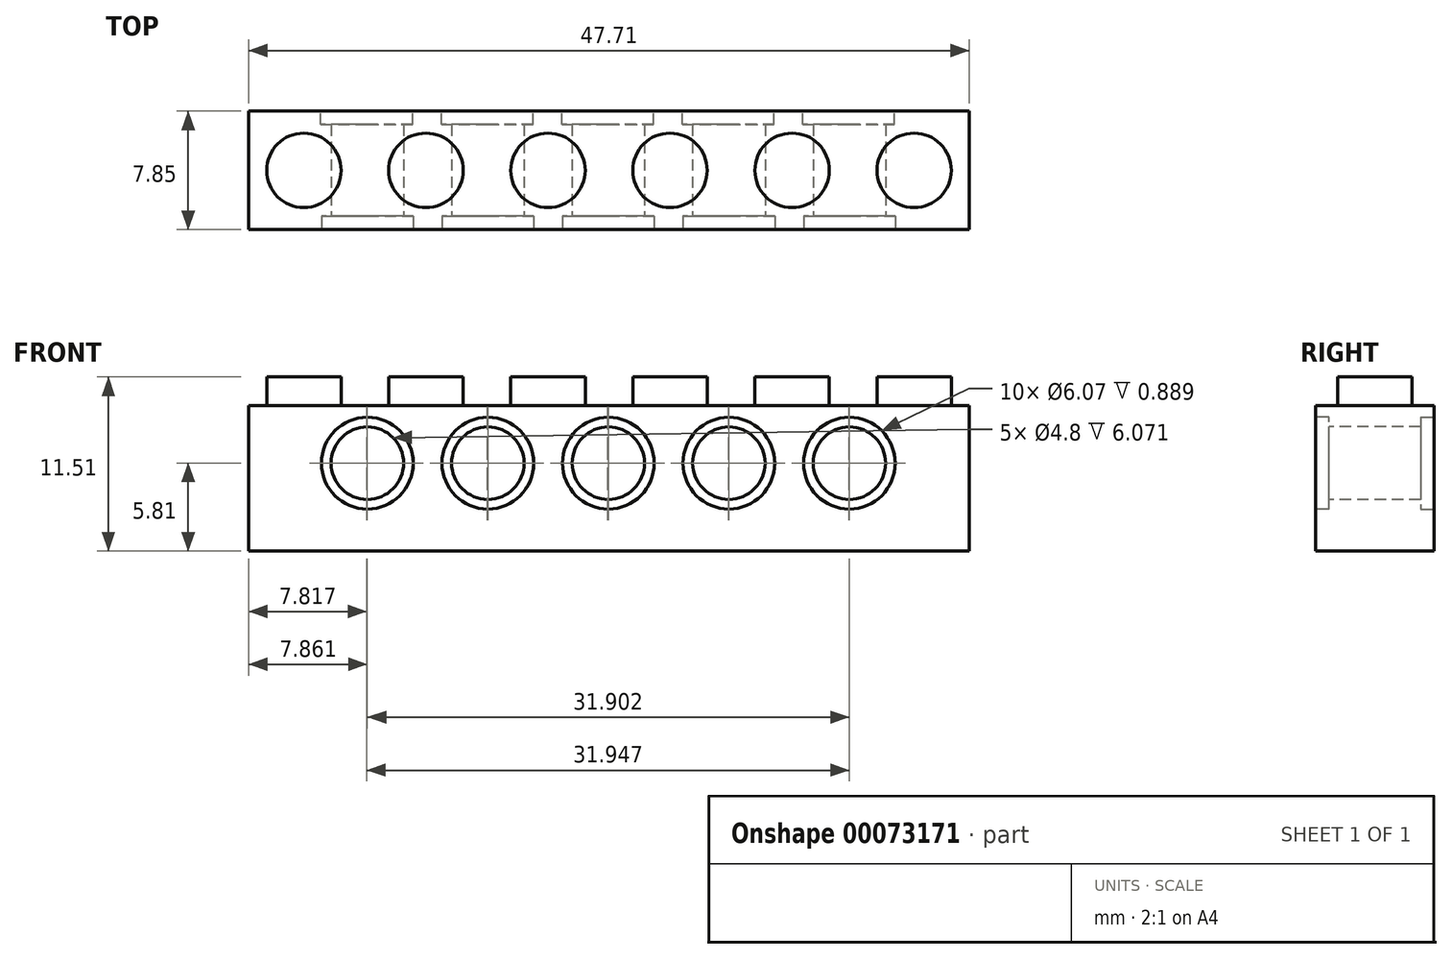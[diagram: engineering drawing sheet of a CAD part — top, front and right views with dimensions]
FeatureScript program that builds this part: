
annotation { "Feature Type Name" : "Feature", "Feature Type Description" : "" }
export const myFeature = defineFeature(function(context is Context, id is Id, definition is map)
    precondition{}
    {
        {
            var Q0;
            Q0=qCreatedBy(makeId("Front.planeOp"),FACE);
            var sketch = newSketch(context, id + "F0", { "sketchPlane" : qUnion([Q0])});
            skLineSegment(sketch, "E0.bottom", {"start": v(-30.48, 15.74) * mm, "end": v(17.23, 15.74) * mm});
            skLineSegment(sketch, "E0.top", {"start": v(-30.48, 6.13) * mm, "end": v(17.23, 6.13) * mm});
            skLineSegment(sketch, "E0.left", {"start": v(-30.48, 15.74) * mm, "end": v(-30.48, 6.13) * mm});
            skLineSegment(sketch, "E0.right", {"start": v(17.23, 15.74) * mm, "end": v(17.23, 6.13) * mm});
            skSolve(sketch);
        }
        {
            var Q0;
            Q0 = qSketchRegion(id + "F0", true);
            extrude(context, id + "F1", {"entities" : qUnion([Q0]), "depth" : 7.85 * mm});
        }
        {
            var Q0;
            Q0=makeQuery(id+"F1.opExtrude","CAP_FACE",FACE,{"disambiguationData":[OSD([sQuery(id+"F0.wireOp",EDGE,"E0.bottom"),sQuery(id+"F0.wireOp",EDGE,"E0.top"),sQuery(id+"F0.wireOp",EDGE,"E0.left"),sQuery(id+"F0.wireOp",EDGE,"E0.right")])],"isStart":false});
            var sketch = newSketch(context, id + "F2", { "sketchPlane" : qUnion([Q0])});
            skCircle(sketch, "E1", {"center": v(-22.62, 11.94) * mm, "radius": 3.04 * mm});
            skPoint(sketch, "E2.centerSnap0", {"position": v(-30.48, 10.93) * mm});
            skCircle(sketch, "E3", {"center": v(-14.64, 11.94) * mm, "radius": 3.04 * mm});
            skCircle(sketch, "E4", {"center": v(-6.67, 11.94) * mm, "radius": 3.04 * mm});
            skCircle(sketch, "E5", {"center": v(1.3, 11.94) * mm, "radius": 3.04 * mm});
            skCircle(sketch, "E6", {"center": v(9.28, 11.94) * mm, "radius": 3.04 * mm});
            skSolve(sketch);
        }
        {
            var Q0;
            Q0 = qSketchRegion(id + "F2", true);
            extrude(context, id + "F3", {"entities" : qUnion([Q0]), "operationType" : NewBodyOperationType.REMOVE, "oppositeDirection" : true, "depth" : 0.89 * mm});
        }
        {
            var Q0;
            Q0=makeQuery(id+"F1.opExtrude","CAP_FACE",FACE,{"disambiguationData":[OSD([sQuery(id+"F0.wireOp",EDGE,"E0.bottom"),sQuery(id+"F0.wireOp",EDGE,"E0.top"),sQuery(id+"F0.wireOp",EDGE,"E0.left"),sQuery(id+"F0.wireOp",EDGE,"E0.right")])],"isStart":true});
            var sketch = newSketch(context, id + "F4", { "sketchPlane" : qUnion([Q0])});
            skCircle(sketch, "E7", {"center": v(-9.24, 11.94) * mm, "radius": 3.04 * mm});
            skCircle(sketch, "E8", {"center": v(-1.26, 11.94) * mm, "radius": 3.04 * mm});
            skCircle(sketch, "E9", {"center": v(6.71, 11.94) * mm, "radius": 3.04 * mm});
            skCircle(sketch, "E10", {"center": v(14.69, 11.94) * mm, "radius": 3.04 * mm});
            skCircle(sketch, "E11", {"center": v(22.66, 11.94) * mm, "radius": 3.04 * mm});
            skSolve(sketch);
        }
        {
            var Q0;
            Q0 = qSketchRegion(id + "F4", true);
            extrude(context, id + "F5", {"entities" : qUnion([Q0]), "operationType" : NewBodyOperationType.REMOVE, "oppositeDirection" : true, "depth" : 0.89 * mm});
        }
        {
            var Q0;
            Q0=makeQuery(id+"F1.opExtrude","CAP_FACE",FACE,{"disambiguationData":[OSD([sQuery(id+"F0.wireOp",EDGE,"E0.bottom"),sQuery(id+"F0.wireOp",EDGE,"E0.top"),sQuery(id+"F0.wireOp",EDGE,"E0.left"),sQuery(id+"F0.wireOp",EDGE,"E0.right")])],"isStart":false});
            var sketch = newSketch(context, id + "F6", { "sketchPlane" : qUnion([Q0])});
            skCircle(sketch, "E12", {"center": v(-22.62, 11.94) * mm, "radius": 2.4 * mm});
            skCircle(sketch, "E13", {"center": v(-14.64, 11.94) * mm, "radius": 2.4 * mm});
            skCircle(sketch, "E14", {"center": v(-6.67, 11.94) * mm, "radius": 2.4 * mm});
            skCircle(sketch, "E15", {"center": v(1.3, 11.94) * mm, "radius": 2.4 * mm});
            skCircle(sketch, "E16", {"center": v(9.28, 11.94) * mm, "radius": 2.4 * mm});
            skSolve(sketch);
        }
        {
            var Q0;
            Q0 = qSketchRegion(id + "F6", true);
            extrude(context, id + "F7", {"entities" : qUnion([Q0]), "operationType" : NewBodyOperationType.REMOVE, "endBound" : BoundingType.THROUGH_ALL, "oppositeDirection" : true, "depth" : 25.4 * mm});
        }
        {
            var Q0;
            Q0=makeQuery(id+"F1.opExtrude","SWEPT_FACE",FACE,{"disambiguationData":[OSD([sQuery(id+"F0.wireOp",EDGE,"E0.bottom")])]});
            var sketch = newSketch(context, id + "F8", { "sketchPlane" : qUnion([Q0])});
            skCircle(sketch, "E17", {"center": v(-26.82, -3.92) * mm, "radius": 2.46 * mm});
            skLineSegment(sketch, "E18", {"start": v(-26.82, -3.92) * mm, "end": v(-26.82, 0) * mm, "construction": true});
            skLineSegment(sketch, "E19", {"start": v(-26.82, -3.92) * mm, "end": v(-26.82, -7.85) * mm, "construction": true});
            skCircle(sketch, "E20", {"center": v(-18.74, -3.92) * mm, "radius": 2.46 * mm});
            skLineSegment(sketch, "E21", {"start": v(-18.74, -3.92) * mm, "end": v(-18.74, 0) * mm, "construction": true});
            skLineSegment(sketch, "E22", {"start": v(-18.74, -3.92) * mm, "end": v(-18.74, -7.85) * mm, "construction": true});
            skCircle(sketch, "E23", {"center": v(-10.66, -3.92) * mm, "radius": 2.46 * mm});
            skLineSegment(sketch, "E24", {"start": v(-10.66, -3.92) * mm, "end": v(-10.66, 0) * mm, "construction": true});
            skLineSegment(sketch, "E25", {"start": v(-10.66, -3.92) * mm, "end": v(-10.66, -7.85) * mm, "construction": true});
            skCircle(sketch, "E26", {"center": v(-2.59, -3.92) * mm, "radius": 2.46 * mm});
            skLineSegment(sketch, "E27", {"start": v(-2.59, -3.92) * mm, "end": v(-2.59, 0) * mm, "construction": true});
            skLineSegment(sketch, "E28", {"start": v(-2.59, -3.92) * mm, "end": v(-2.59, -7.85) * mm, "construction": true});
            skCircle(sketch, "E29", {"center": v(5.49, -3.92) * mm, "radius": 2.46 * mm});
            skLineSegment(sketch, "E30", {"start": v(5.49, -3.92) * mm, "end": v(5.49, 0) * mm, "construction": true});
            skLineSegment(sketch, "E31", {"start": v(5.49, -3.92) * mm, "end": v(5.49, -7.85) * mm, "construction": true});
            skCircle(sketch, "E32", {"center": v(13.57, -3.92) * mm, "radius": 2.46 * mm});
            skLineSegment(sketch, "E33", {"start": v(13.57, -3.92) * mm, "end": v(13.57, 0) * mm, "construction": true});
            skLineSegment(sketch, "E34", {"start": v(13.57, -3.92) * mm, "end": v(13.57, -7.85) * mm, "construction": true});
            skLineSegment(sketch, "E35", {"start": v(-30.48, -3.92) * mm, "end": v(-26.82, -3.92) * mm, "construction": true});
            skLineSegment(sketch, "E36", {"start": v(13.57, -3.92) * mm, "end": v(17.23, -3.92) * mm, "construction": true});
            skSolve(sketch);
        }
        {
            var Q0;
            Q0 = qSketchRegion(id + "F8", true);
            extrude(context, id + "F9", {"entities" : qUnion([Q0]), "operationType" : NewBodyOperationType.ADD, "depth" : 1.9 * mm});
        }
    });
